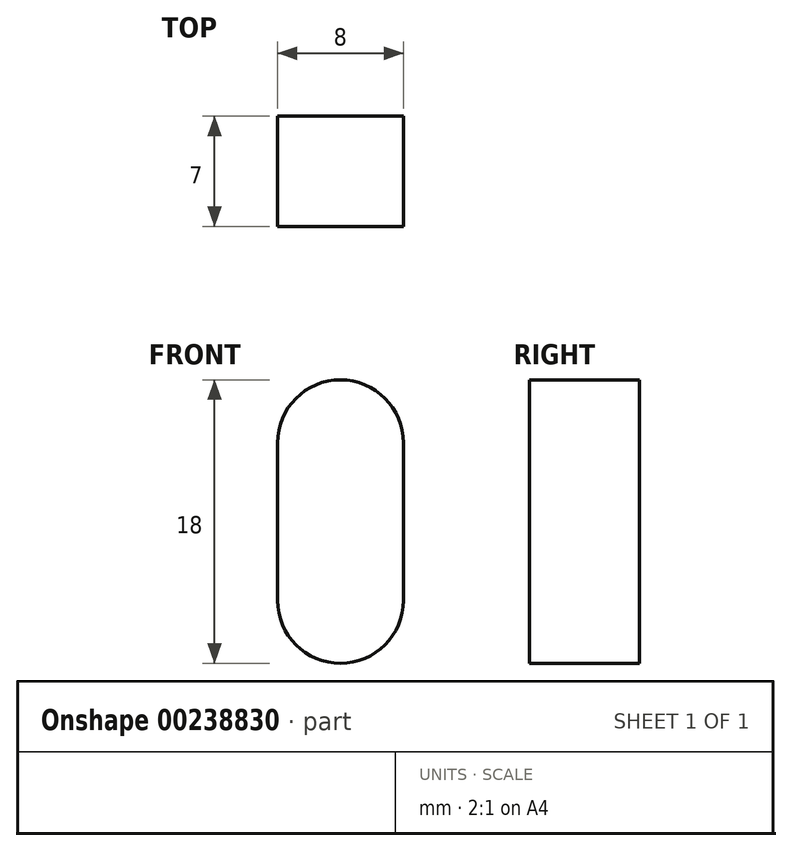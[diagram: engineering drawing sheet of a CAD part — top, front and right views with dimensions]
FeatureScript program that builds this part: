
annotation { "Feature Type Name" : "Feature", "Feature Type Description" : "" }
export const myFeature = defineFeature(function(context is Context, id is Id, definition is map)
    precondition{}
    {
        {
            var Q0;
            Q0=qCreatedBy(makeId("Front.planeOp"),FACE);
            var sketch = newSketch(context, id + "F0", { "sketchPlane" : qUnion([Q0])});
            skLineSegment(sketch, "E0.bottom", {"start": v(-4, 0) * mm, "end": v(4, 0) * mm});
            skLineSegment(sketch, "E0.top", {"start": v(-4, -10) * mm, "end": v(4, -10) * mm});
            skLineSegment(sketch, "E0.left", {"start": v(-4, 0) * mm, "end": v(-4, -10) * mm});
            skLineSegment(sketch, "E0.right", {"start": v(4, 0) * mm, "end": v(4, -10) * mm});
            skArc(sketch, "E1", {"start": v(4, 0) * mm, "mid": v(0, 4) * mm, "end": v(-4, 0) * mm});
            skArc(sketch, "E2", {"start": v(-4, -10) * mm, "mid": v(0, -14) * mm, "end": v(4, -10) * mm});
            skSolve(sketch);
        }
        {
            var Q0;
            Q0=makeQuery(id+"F0.imprint","IMPRINT",FACE,{"disambiguationData":[TD([[makeQuery(id+"F0.imprint","IMPRINT",EDGE,{"derivedFrom":sQuery(id+"F0.wireOp",EDGE,"E0.bottom")}),1.0]])]});
            var Q1;
            Q1=makeQuery(id+"F0.imprint","IMPRINT",FACE,{"disambiguationData":[TD([[makeQuery(id+"F0.imprint","IMPRINT",EDGE,{"derivedFrom":sQuery(id+"F0.wireOp",EDGE,"E0.bottom")}),-1.0]])]});
            var Q2;
            Q2=makeQuery(id+"F0.imprint","IMPRINT",FACE,{"disambiguationData":[TD([[makeQuery(id+"F0.imprint","IMPRINT",EDGE,{"derivedFrom":sQuery(id+"F0.wireOp",EDGE,"E0.top")}),-1.0]])]});
            extrude(context, id + "F1", {"entities" : qUnion([Q0, Q1, Q2]), "depth" : 7 * mm});
        }
    });
